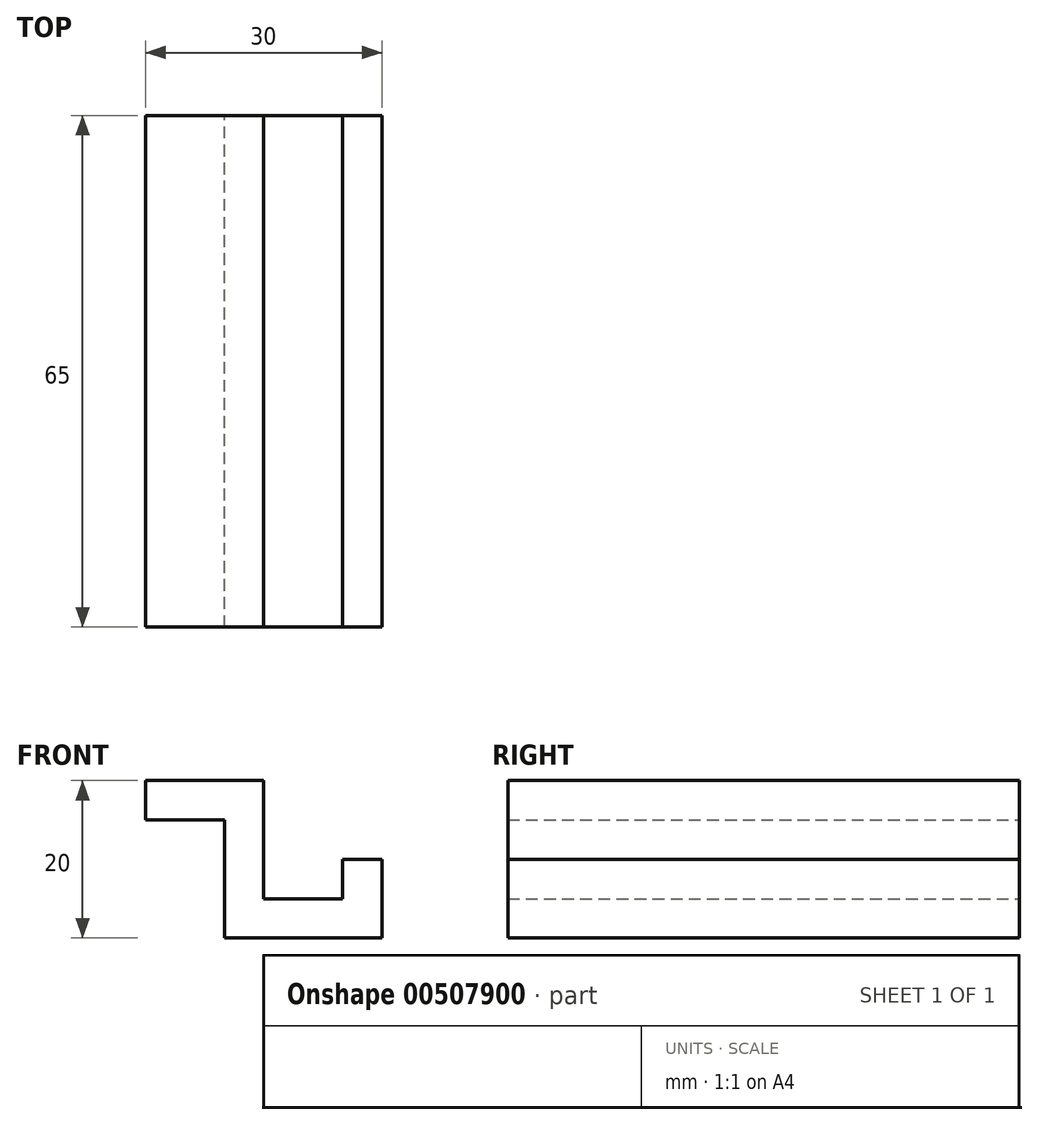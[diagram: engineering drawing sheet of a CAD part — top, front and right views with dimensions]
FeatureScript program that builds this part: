
annotation { "Feature Type Name" : "Feature", "Feature Type Description" : "" }
export const myFeature = defineFeature(function(context is Context, id is Id, definition is map)
    precondition{}
    {
        {
            var Q0;
            Q0=qCreatedBy(makeId("Front.planeOp"),FACE);
            var sketch = newSketch(context, id + "F0", { "sketchPlane" : qUnion([Q0])});
            skLineSegment(sketch, "E0", {"start": v(0, 0) * mm, "end": v(11.12, 0) * mm, "construction": true});
            skLineSegment(sketch, "E1", {"start": v(0, 0) * mm, "end": v(0, 15) * mm});
            skLineSegment(sketch, "E2", {"start": v(0, 15) * mm, "end": v(-10, 15) * mm});
            skLineSegment(sketch, "E3", {"start": v(-10, 15) * mm, "end": v(-10, 20) * mm});
            skLineSegment(sketch, "E4", {"start": v(-10, 20) * mm, "end": v(5, 20) * mm});
            skLineSegment(sketch, "E5", {"start": v(5, 20) * mm, "end": v(5, 5) * mm});
            skLineSegment(sketch, "E6", {"start": v(5, 5) * mm, "end": v(15, 5) * mm});
            skLineSegment(sketch, "E7", {"start": v(15, 5) * mm, "end": v(15, 10) * mm});
            skLineSegment(sketch, "E8", {"start": v(15, 10) * mm, "end": v(20, 10) * mm});
            skLineSegment(sketch, "E9", {"start": v(20, 10) * mm, "end": v(20, 0) * mm});
            skLineSegment(sketch, "E10", {"start": v(20, 0) * mm, "end": v(0, 0) * mm});
            skSolve(sketch);
        }
        {
            var Q0;
            Q0=makeQuery(id+"F0.imprint","IMPRINT",FACE,{"disambiguationData":[TD([[makeQuery(id+"F0.imprint","IMPRINT",EDGE,{"derivedFrom":sQuery(id+"F0.wireOp",EDGE,"E1")}),-1.0]])]});
            extrude(context, id + "F1", {"entities" : qUnion([Q0]), "depth" : 65 * mm, "offsetDistance" : 25 * mm});
        }
    });
